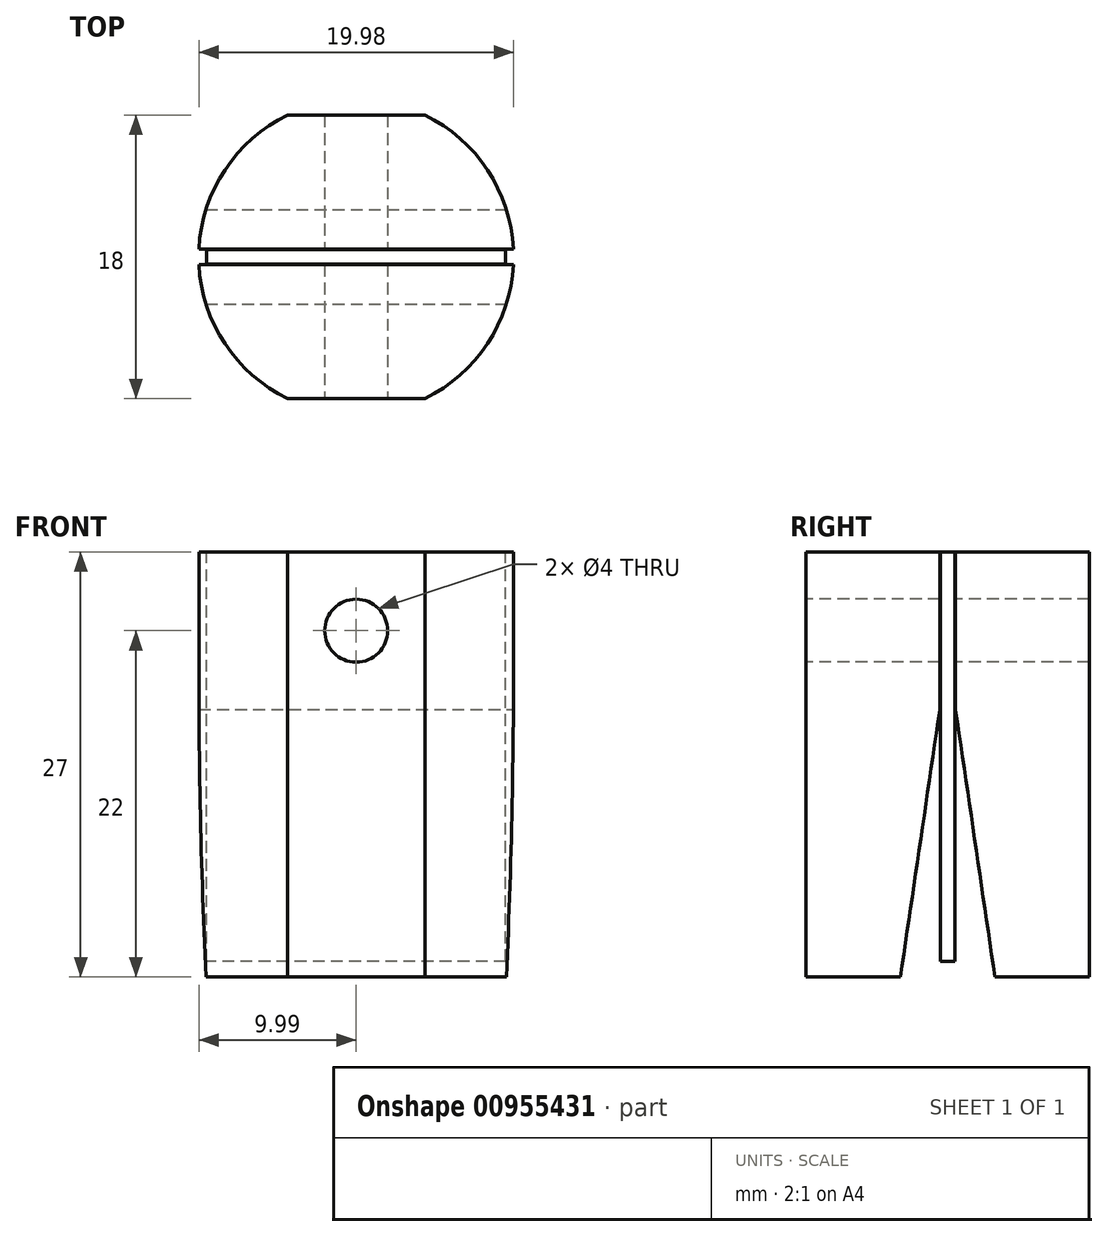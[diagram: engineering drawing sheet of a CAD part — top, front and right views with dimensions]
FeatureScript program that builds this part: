
annotation { "Feature Type Name" : "Feature", "Feature Type Description" : "" }
export const myFeature = defineFeature(function(context is Context, id is Id, definition is map)
    precondition{}
    {
        {
            var Q0;
            Q0=qCreatedBy(makeId("Top.planeOp"),FACE);
            var sketch = newSketch(context, id + "F0", { "sketchPlane" : qUnion([Q0])});
            skCircle(sketch, "E0", {"center": v(0, 0) * mm, "radius": 10 * mm});
            skSolve(sketch);
        }
        {
            var Q0;
            Q0 = qSketchRegion(id + "F0", true);
            extrude(context, id + "F1", {"entities" : qUnion([Q0]), "depth" : 25 * mm, "offsetDistance" : 25 * mm});
        }
        {
            var Q0;
            Q0=qCreatedBy(makeId("Right.planeOp"),FACE);
            var sketch = newSketch(context, id + "F2", { "sketchPlane" : qUnion([Q0])});
            skPoint(sketch, "E1", {"position": v(0, 25) * mm});
            skLineSegment(sketch, "E2", {"start": v(3, 8) * mm, "end": v(-3, 8) * mm});
            skLineSegment(sketch, "E3", {"start": v(0.5, 25) * mm, "end": v(-0.5, 25) * mm});
            skLineSegment(sketch, "E4", {"start": v(3, 8) * mm, "end": v(0.5, 25) * mm});
            skLineSegment(sketch, "E5", {"start": v(-0.5, 25) * mm, "end": v(-3, 8) * mm});
            skSolve(sketch);
        }
        {
            var Q0;
            Q0 = qSketchRegion(id + "F2", true);
            extrude(context, id + "F3", {"entities" : qUnion([Q0]), "operationType" : NewBodyOperationType.REMOVE, "endBound" : BoundingType.SYMMETRIC, "oppositeDirection" : true, "depth" : 25 * mm, "offsetDistance" : 25 * mm});
        }
        {
            var Q0;
            {var subQ0=sQuery(id+"F0.wireOp",EDGE,"E0");Q0=makeQuery(id+"F3.boolean.opBoolean","SPLIT",FACE,{"disambiguationData":[TD([makeQuery(id+"F3.opExtrude","SWEPT_FACE",FACE,{"disambiguationData":[OSD([sQuery(id+"F2.wireOp",EDGE,"E4")])]})])],"derivedFrom":makeQuery(id+"F1.opExtrude","CAP_FACE",FACE,{"disambiguationData":[OSD([subQ0])],"isStart":false})});}
            var Q1;
            {var subQ0=sQuery(id+"F0.wireOp",EDGE,"E0");Q1=makeQuery(id+"F3.boolean.opBoolean","SPLIT",FACE,{"disambiguationData":[TD([makeQuery(id+"F3.opExtrude","SWEPT_FACE",FACE,{"disambiguationData":[OSD([sQuery(id+"F2.wireOp",EDGE,"E5")])]})])],"derivedFrom":makeQuery(id+"F1.opExtrude","CAP_FACE",FACE,{"disambiguationData":[OSD([subQ0])],"isStart":false})});}
            extrude(context, id + "F4", {"entities" : qUnion([Q0, Q1]), "operationType" : NewBodyOperationType.ADD, "depth" : 10 * mm, "offsetDistance" : 25 * mm});
        }
        {
            var Q0;
            Q0=qCreatedBy(makeId("Right.planeOp"),FACE);
            var sketch = newSketch(context, id + "F5", { "sketchPlane" : qUnion([Q0])});
            skLineSegment(sketch, "E6", {"start": v(-21.51, 8) * mm, "end": v(29.14, 8) * mm});
            skLineSegment(sketch, "E7", {"start": v(29.14, 8) * mm, "end": v(29.87, -10.93) * mm});
            skLineSegment(sketch, "E8", {"start": v(29.87, -10.93) * mm, "end": v(-21.96, -11.83) * mm});
            skLineSegment(sketch, "E9", {"start": v(-21.96, -11.83) * mm, "end": v(-21.51, 8) * mm});
            skSolve(sketch);
        }
        {
            var Q0;
            Q0=makeQuery(id+"F5.imprint","IMPRINT",FACE,{"disambiguationData":[TD([[makeQuery(id+"F5.imprint","IMPRINT",EDGE,{"derivedFrom":sQuery(id+"F5.wireOp",EDGE,"E6")}),-1.0]])]});
            extrude(context, id + "F6", {"entities" : qUnion([Q0]), "operationType" : NewBodyOperationType.REMOVE, "endBound" : BoundingType.SYMMETRIC, "oppositeDirection" : true, "depth" : 25 * mm, "offsetDistance" : 25 * mm});
        }
        {
            var Q0;
            Q0=qCreatedBy(makeId("Front.planeOp"),FACE);
            var sketch = newSketch(context, id + "F7", { "sketchPlane" : qUnion([Q0])});
            skCircle(sketch, "E10", {"center": v(0, 30) * mm, "radius": 2 * mm});
            skSolve(sketch);
        }
        {
            var Q0;
            Q0 = qSketchRegion(id + "F7", true);
            extrude(context, id + "F8", {"entities" : qUnion([Q0]), "operationType" : NewBodyOperationType.REMOVE, "endBound" : BoundingType.SYMMETRIC, "oppositeDirection" : true, "depth" : 25 * mm, "offsetDistance" : 25 * mm});
        }
        {
            var Q0;
            {var subQ0=sQuery(id+"F0.wireOp",EDGE,"E0");Q0=makeQuery(id+"F4.opExtrude","CAP_FACE",FACE,{"disambiguationData":[OSD([subQ0]),TDD([makeQuery(id+"F3.boolean.opBoolean","SPLIT",FACE,{"disambiguationData":[TD([makeQuery(id+"F3.opExtrude","SWEPT_FACE",FACE,{"disambiguationData":[OSD([sQuery(id+"F2.wireOp",EDGE,"E4")])]})])],"derivedFrom":makeQuery(id+"F1.opExtrude","CAP_FACE",FACE,{"disambiguationData":[OSD([subQ0])],"isStart":false})})])],"isStart":false});}
            var sketch = newSketch(context, id + "F9", { "sketchPlane" : qUnion([Q0])});
            skLineSegment(sketch, "E11.bottom", {"start": v(9.5, 0.45) * mm, "end": v(-9.5, 0.45) * mm});
            skLineSegment(sketch, "E11.top", {"start": v(9.5, -0.45) * mm, "end": v(-9.5, -0.45) * mm});
            skLineSegment(sketch, "E11.left", {"start": v(9.5, 0.45) * mm, "end": v(9.5, -0.45) * mm});
            skLineSegment(sketch, "E11.right", {"start": v(-9.5, 0.45) * mm, "end": v(-9.5, -0.45) * mm});
            skPoint(sketch, "E11.middle", {"position": v(0, 0) * mm});
            skSolve(sketch);
        }
        {
            var Q0;
            Q0 = qSketchRegion(id + "F9", true);
            extrude(context, id + "F10", {"entities" : qUnion([Q0]), "oppositeDirection" : true, "depth" : 26 * mm, "offsetDistance" : 25 * mm});
        }
        {
            var Q0;
            {var subQ2=makeQuery(id+"F3.opExtrude","SWEPT_FACE",FACE,{"disambiguationData":[OSD([sQuery(id+"F2.wireOp",EDGE,"E5")])]});Q0=makeQuery(id+"F6.boolean.opBoolean","COPY",FACE,{"disambiguationData":[TD([makeQuery(id+"F3.boolean.opBoolean","COPY",FACE,{"derivedFrom":subQ2})])],"derivedFrom":makeQuery(id+"F6.opExtrude","SWEPT_FACE",FACE,{"disambiguationData":[OSD([sQuery(id+"F5.wireOp",EDGE,"E6")])]})});}
            var sketch = newSketch(context, id + "F11", { "sketchPlane" : qUnion([Q0])});
            skLineSegment(sketch, "E12.top", {"start": v(-17.87, -9) * mm, "end": v(19.68, -9) * mm});
            skLineSegment(sketch, "E12.left", {"start": v(-17.87, 9) * mm, "end": v(-17.87, -9) * mm});
            skLineSegment(sketch, "E12.right", {"start": v(19.68, 9) * mm, "end": v(19.68, -9) * mm});
            skLineSegment(sketch, "E13.bottom", {"start": v(-27.76, 14.82) * mm, "end": v(34.8, 14.82) * mm});
            skLineSegment(sketch, "E13.top", {"start": v(-27.76, -14.43) * mm, "end": v(34.8, -14.43) * mm});
            skLineSegment(sketch, "E13.left", {"start": v(-27.76, 14.82) * mm, "end": v(-27.76, -14.43) * mm});
            skLineSegment(sketch, "E13.right", {"start": v(34.8, 14.82) * mm, "end": v(34.8, -14.43) * mm});
            skLineSegment(sketch, "E14", {"start": v(-17.87, 9) * mm, "end": v(19.68, 9) * mm});
            skSolve(sketch);
        }
        {
            var Q0;
            Q0 = qSketchRegion(id + "F11", true);
            extrude(context, id + "F12", {"entities" : qUnion([Q0]), "operationType" : NewBodyOperationType.REMOVE, "oppositeDirection" : true, "depth" : 30 * mm, "offsetDistance" : 25 * mm});
        }
    });
